# Revit family: 1030082(n0300)
name_source: partatom
category: Security Devices
units: mm (PartAtom-declared; Revit-internal decimal feet)

## family parameters
Always vertical = No
Cut with Voids When Loaded = No
Host = Ceiling
OmniClass Number = 23.85.30.14
OmniClass Title = Presence Detection/Registration
Room Calculation Point = No
Shared = Yes

## types (2) — shared parameters
zero-valued in all types: A

## per-type parameters (varying)
- Type 1: CTN=0; EF000008=0 mm  [stored 0 ft]; EF000040=0 mm  [stored 0 ft]; EF000049=0 mm  [stored 0 ft]; EF000194=0; EF000218=0 mm  [stored 0 ft]; EF000551=0 mm  [stored 0 ft]; EF000846=0 mm  [stored 0 ft]; EF001322=0 mm  [stored 0 ft]; EF001323=0 mm  [stored 0 ft]; EF003843=0 mm  [stored 0 ft]; EF003882=0; EF004101=0.00°; EF004265=0 mm  [stored 0 ft]; EF006589=0; EF006590=0; EF008011=0 mm  [stored 0 ft]; EF010886=0 mm  [stored 0 ft]; EF010945=0 mm  [stored 0 ft]; EF010946=0 mm  [stored 0 ft]; LOG=0; NOCUPEROU=0; PRICEQUANTITY=0; QUANTITYINT=0; QUANTITYMIN=0
- 1030082: ARTICLENO=NB; BOMINFO=LINA; CATALOG=Theben; COO=CN; CTN=85365080; DEEPLINK_PRODUKTSEITE=http://www.theben.de; DESCLONG=Passive infrared presence detector for surface ceiling mounting, Rectangular detection area 360° for corridors, 28x5 m, (140 square meters) at 3 m mounting height (transverse walking), 14x5 m, (70 square meters) at 3 m mounting height (frontal walking), 1 channel light (relay 230 V), Can also be used in damp rooms and outdoors due to protection class IP 54, Can be remote controlled, Parallel connection with other LUXA 103 or theMura Slave possible, Switching capacity optimized for LED up to 400 W, Semi- or fully automatic operation, Integrated push-button input, with pulse function, teach-in function, test function and staircase lighting function, Area restriction possible with cover clips, Housing color white, Surface-mounted frame in black or gray available as separate accessory; DESCSHORT=Corridor presence detector ceiling mount surface, detection area 28x5 m, 1 x light; EF000003=EV000384; EF000007=White; EF000008=94 mm  [stored 0.308399 ft]; EF000010=Presence detector; EF000025=true; EF000040=58 mm  [stored 0.190289 ft]; EF000049=94 mm  [stored 0.308399 ft]; EF000124=Screw clamp; EF000139=Untreated; EF000147=false; EF000187=AC; EF000194=15; EF000218=1 mm  [stored 0.00328084 ft]; EF000416=50, 50 Hz; EF000483=false; EF000551=94 mm  [stored 0.308399 ft]; EF000846=1 mm  [stored 0.00328084 ft]; EF001098=true; EF001099=true; EF001198=false; EF001257=Thermoplast; EF001322=14000 mm; EF001323=14000 mm; EF001731=-25, 55 °C; EF002169=Plastic; EF003429=true; EF003808=false; EF003814=5, 1000 lx; EF003832=false; EF003843=140000 mm; EF003848=true; EF003858=false; EF003863=false; EF003876=true; EF003882=9010; EF003890=true; EF003898=true; EF003904=true; EF003920=false; EF004101=360.00°; EF004265=15 mm  [stored 0.0492126 ft]; EF004293=IK04; EF005474=IP54; EF005624=false; EF006243=false; EF006311=false; EF006569=matt; EF006582=0, 360 °; EF006589=15; EF006590=30; EF006644=false; EF007575=true; EF008011=3000 mm; EF009569=false; EF010886=58 mm  [stored 0.190289 ft]; EF010945=94 mm  [stored 0.308399 ft]; EF010946=55 mm  [stored 0.180446 ft]; EF011072=false; EF011991=false; EF014925=false; EF014926=false; EF014927=false; EF020270=Passive infrared; EF021180=true; EF023790=false; GEBRAUCHSANLEITUNG=http://www.theben.de; INTNO=4003468101780; LINA=1030082; LOG=300; MANUID=1030082; MANUNAME=Theben AG; MANUTYPEDESC=LUXA 103 S360-100-28 AP WH; Manufacturer=Theben; Model=1030082; NB=1030082(N0300); NBSYN=$MANUID.($SA.$A.$LOG.); NN=LUXA 103; NOCUPEROU=1; PRICEQUANTITY=1; PRODUKTDATENBLATT=http://www.theben.de; QUANTITYINT=1; QUANTITYMIN=1; REACH_ERKLAERUNG=http://www.theben.de; REMARKS=ERP-GROUP 450; SA=None; SUPPLIER=THEBEN; SUPPLIERALTNO=1030082

note: [stored X ft] marks values corroborated as IEEE doubles in the binary element streams (Revit-internal decimal feet)

## geometry (parser evidence)
native form markers: Sweep x10
no freeform markers — native parametric forms only
